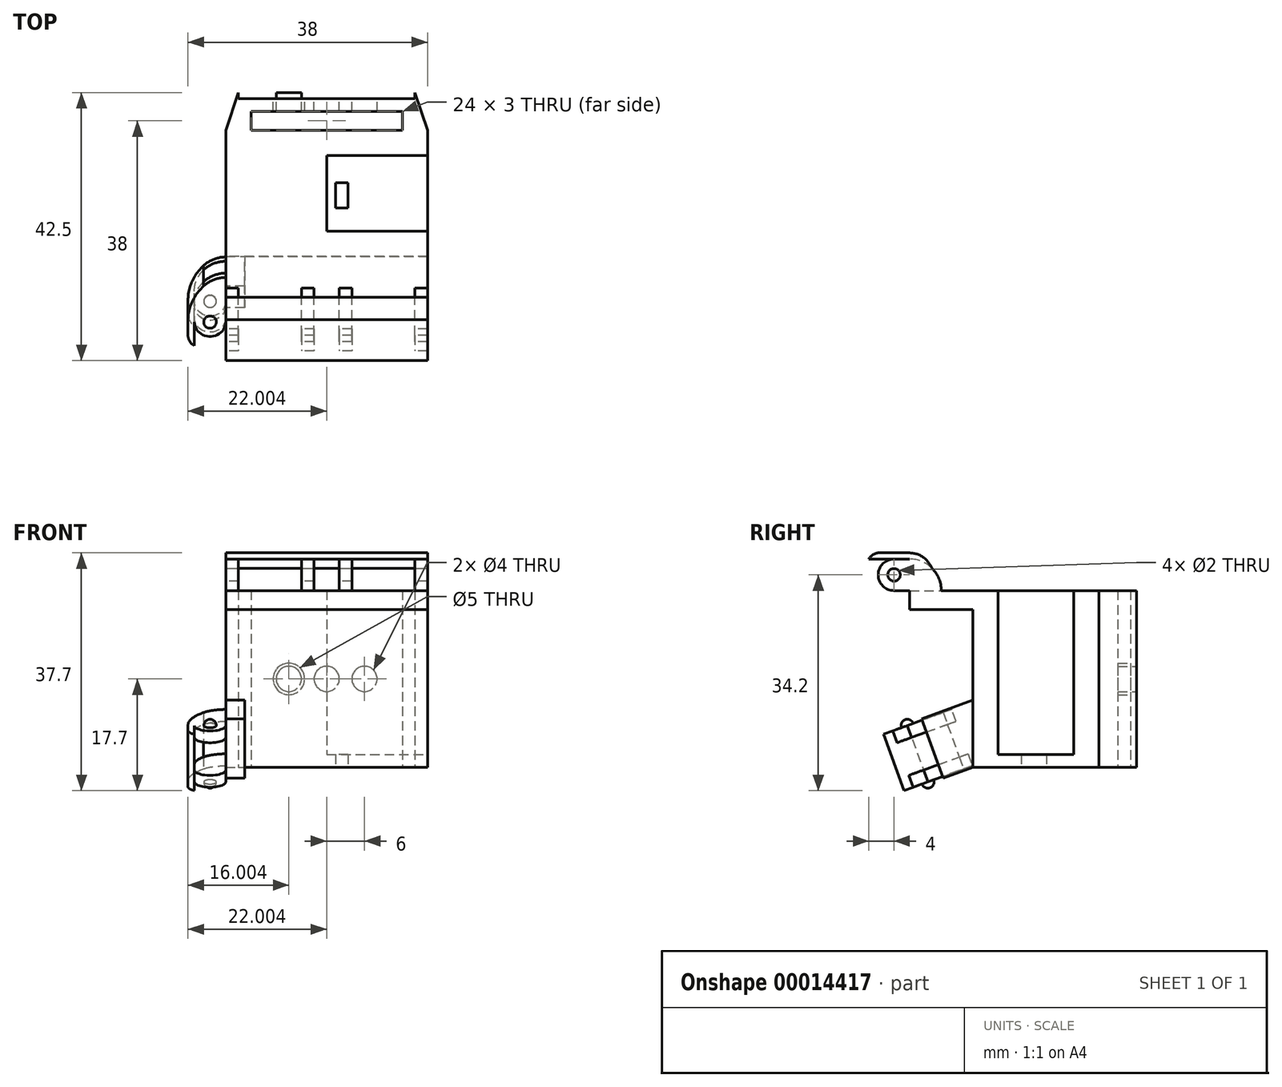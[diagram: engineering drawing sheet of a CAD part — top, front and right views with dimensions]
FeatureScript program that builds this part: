
annotation { "Feature Type Name" : "Feature", "Feature Type Description" : "" }
export const myFeature = defineFeature(function(context is Context, id is Id, definition is map)
    precondition{}
    {
        {
            var Q0;
            Q0=qCreatedBy(makeId("Top.planeOp"),FACE);
            var sketch = newSketch(context, id + "F0", { "sketchPlane" : qUnion([Q0])});
            skLineSegment(sketch, "E0.0", {"start": v(-15.62, 10.4) * mm, "end": v(16.38, 10.4) * mm});
            skLineSegment(sketch, "E0.1", {"start": v(-15.62, 10.4) * mm, "end": v(-15.62, -9.6) * mm});
            skLineSegment(sketch, "E0.2", {"start": v(-15.62, -9.6) * mm, "end": v(16.38, -9.6) * mm});
            skLineSegment(sketch, "E0.3", {"start": v(16.38, 10.4) * mm, "end": v(16.38, -9.6) * mm});
            skLineSegment(sketch, "E1", {"start": v(0.38, 10.4) * mm, "end": v(0.38, 16) * mm, "construction": true});
            skPoint(sketch, "E2", {"position": v(0.38, 13.4) * mm});
            skPoint(sketch, "E3", {"position": v(12.38, 10.4) * mm});
            skLineSegment(sketch, "E4", {"start": v(12.38, 10.4) * mm, "end": v(12.38, 13.4) * mm});
            skLineSegment(sketch, "E5", {"start": v(0.38, 13.4) * mm, "end": v(12.38, 13.4) * mm});
            skLineSegment(sketch, "E6.MirrorCS", {"start": v(0.38, 13.4) * mm, "end": v(-11.62, 13.4) * mm});
            skLineSegment(sketch, "E7.MirrorCS", {"start": v(-11.62, 10.4) * mm, "end": v(-11.62, 13.4) * mm});
            skPoint(sketch, "E8", {"position": v(0.38, 16.4) * mm});
            skLineSegment(sketch, "E9", {"start": v(0.38, 16.4) * mm, "end": v(14.38, 16.4) * mm});
            skLineSegment(sketch, "E10", {"start": v(16.38, 10.4) * mm, "end": v(14.38, 16.4) * mm});
            skLineSegment(sketch, "E11.MirrorCS", {"start": v(0.38, 16.4) * mm, "end": v(-13.62, 16.4) * mm});
            skLineSegment(sketch, "E12.MirrorCS", {"start": v(-15.62, 10.4) * mm, "end": v(-13.62, 16.4) * mm});
            skLineSegment(sketch, "E13", {"start": v(16.38, -5.6) * mm, "end": v(0.38, -5.6) * mm});
            skLineSegment(sketch, "E14", {"start": v(0.38, -5.6) * mm, "end": v(0.38, 6.4) * mm});
            skLineSegment(sketch, "E15", {"start": v(0.38, 6.4) * mm, "end": v(16.38, 6.4) * mm});
            skSolve(sketch);
        }
        {
            var Q0;
            {var subQ2=sQuery(id+"F0.wireOp",EDGE,"E4");Q0=makeQuery(id+"F0.imprint","IMPRINT",FACE,{"disambiguationData":[TD([[makeQuery(id+"F0.imprint","IMPRINT",EDGE,{"derivedFrom":subQ2}),-1.0]])]});}
            var Q1;
            {var subQ0=sQuery(id+"F0.wireOp",EDGE,"E0.1");Q1=makeQuery(id+"F0.imprint","IMPRINT",FACE,{"disambiguationData":[TD([[makeQuery(id+"F0.imprint","IMPRINT",EDGE,{"derivedFrom":subQ0}),1.0]])]});}
            extrude(context, id + "F1", {"entities" : qUnion([Q0, Q1]), "depth" : 28 * mm});
        }
        {
            var Q0;
            Q0=makeQuery(id+"F1.opExtrude","SWEPT_FACE",FACE,{"disambiguationData":[OSD([sQuery(id+"F0.wireOp",EDGE,"E9"),sQuery(id+"F0.wireOp",EDGE,"E11.MirrorCS")])]});
            var sketch = newSketch(context, id + "F2", { "sketchPlane" : qUnion([Q0])});
            skLineSegment(sketch, "E16", {"start": v(-14.88, 14) * mm, "end": v(14.12, 14) * mm, "construction": true});
            skCircle(sketch, "E17", {"center": v(-0.38, 14) * mm, "radius": 2.5 * mm});
            skCircle(sketch, "E18", {"center": v(-0.38, 14) * mm, "radius": 2 * mm});
            skCircle(sketch, "E19", {"center": v(-6.38, 14) * mm, "radius": 2.5 * mm});
            skCircle(sketch, "E20", {"center": v(-6.38, 14) * mm, "radius": 2 * mm});
            skPoint(sketch, "E21", {"position": v(-14.38, 0) * mm});
            skPoint(sketch, "E22", {"position": v(13.62, 0) * mm});
            skLineSegment(sketch, "E23", {"start": v(-14.38, 28) * mm, "end": v(13.62, 0) * mm, "construction": true});
            skLineSegment(sketch, "E24", {"start": v(-14.38, 0) * mm, "end": v(13.62, 28) * mm, "construction": true});
            skLineSegment(sketch, "E25", {"start": v(-0.38, 14) * mm, "end": v(-0.38, 1.54) * mm, "construction": true});
            skCircle(sketch, "E26.MirrorC", {"center": v(5.62, 14) * mm, "radius": 2.5 * mm});
            skCircle(sketch, "E27.MirrorC", {"center": v(5.62, 14) * mm, "radius": 2 * mm});
            skSolve(sketch);
        }
        {
            var Q0;
            Q0=makeQuery(id+"F2.imprint","IMPRINT",FACE,{"disambiguationData":[TD([[makeQuery(id+"F2.imprint","IMPRINT",EDGE,{"derivedFrom":sQuery(id+"F2.wireOp",EDGE,"E20")}),1.0]])]});
            var Q1;
            Q1=makeQuery(id+"F2.imprint","IMPRINT",FACE,{"disambiguationData":[TD([[makeQuery(id+"F2.imprint","IMPRINT",EDGE,{"derivedFrom":sQuery(id+"F2.wireOp",EDGE,"E18")}),1.0]])]});
            var Q2;
            Q2=makeQuery(id+"F2.imprint","IMPRINT",FACE,{"disambiguationData":[TD([[makeQuery(id+"F2.imprint","IMPRINT",EDGE,{"derivedFrom":sQuery(id+"F2.wireOp",EDGE,"20b49b63-29a2-4340-95f1-9f9b38b9fdb5.MirrorC")}),-1.0]])]});
            var Q3;
            Q3=makeQuery(id+"F2.imprint","IMPRINT",FACE,{"disambiguationData":[TD([[makeQuery(id+"F2.imprint","IMPRINT",EDGE,{"derivedFrom":sQuery(id+"F2.wireOp",EDGE,"E27.MirrorC")}),-1.0]])]});
            extrude(context, id + "F3", {"entities" : qUnion([Q0, Q1, Q2, Q3]), "operationType" : NewBodyOperationType.REMOVE, "endBound" : BoundingType.UP_TO_NEXT, "oppositeDirection" : true, "depth" : 25 * mm});
        }
        {
            var Q0;
            Q0=makeQuery(id+"F2.imprint","IMPRINT",FACE,{"disambiguationData":[TD([[makeQuery(id+"F2.imprint","IMPRINT",EDGE,{"derivedFrom":sQuery(id+"F2.wireOp",EDGE,"E19")}),1.0]])]});
            var Q1;
            Q1=makeQuery(id+"F2.imprint","IMPRINT",FACE,{"disambiguationData":[TD([[makeQuery(id+"F2.imprint","IMPRINT",EDGE,{"derivedFrom":sQuery(id+"F2.wireOp",EDGE,"64aa98c8-5af2-4ddf-8823-6346176a8d9f.MirrorC")}),-1.0]])]});
            var Q2;
            Q2=makeQuery(id+"F2.imprint","IMPRINT",FACE,{"disambiguationData":[TD([[makeQuery(id+"F2.imprint","IMPRINT",EDGE,{"derivedFrom":sQuery(id+"F2.wireOp",EDGE,"E17")}),1.0]])]});
            var Q3;
            Q3=makeQuery(id+"F2.imprint","IMPRINT",FACE,{"disambiguationData":[TD([[makeQuery(id+"F2.imprint","IMPRINT",EDGE,{"derivedFrom":sQuery(id+"F2.wireOp",EDGE,"E26.MirrorC")}),-1.0]])]});
            extrude(context, id + "F4", {"entities" : qUnion([Q0, Q1, Q2, Q3]), "operationType" : NewBodyOperationType.REMOVE, "oppositeDirection" : true, "depth" : 1 * mm});
        }
        {
            var Q0;
            Q0=makeQuery(id+"F1.opExtrude","SWEPT_FACE",FACE,{"disambiguationData":[OSD([sQuery(id+"F0.wireOp",EDGE,"E0.2")])]});
            var sketch = newSketch(context, id + "F5", { "sketchPlane" : qUnion([Q0])});
            skPoint(sketch, "E28", {"position": v(-15.62, 28) * mm});
            skPoint(sketch, "E29", {"position": v(-15.62, 25) * mm});
            skPoint(sketch, "E30", {"position": v(-12.62, 28) * mm});
            skLineSegment(sketch, "E31", {"start": v(-12.62, 28) * mm, "end": v(-12.62, 0) * mm, "construction": true});
            skLineSegment(sketch, "E32", {"start": v(-15.62, 25) * mm, "end": v(16.38, 25) * mm, "construction": true});
            skPoint(sketch, "E33", {"position": v(-12.62, 25) * mm});
            skLineSegment(sketch, "E34", {"start": v(16.38, 25) * mm, "end": v(-12.62, 25) * mm});
            skLineSegment(sketch, "E35", {"start": v(-12.62, 0) * mm, "end": v(-12.62, 25) * mm});
            skLineSegment(sketch, "E36", {"start": v(-15.62, 0) * mm, "end": v(-12.62, 0) * mm});
            skLineSegment(sketch, "E37", {"start": v(-15.62, 0) * mm, "end": v(-15.62, 28) * mm});
            skLineSegment(sketch, "E38", {"start": v(-15.62, 28) * mm, "end": v(16.38, 28) * mm});
            skLineSegment(sketch, "E39", {"start": v(16.38, 28) * mm, "end": v(16.38, 25) * mm});
            skSolve(sketch);
        }
        {
            var Q0;
            Q0=makeQuery(id+"F5.imprint","IMPRINT",FACE,{"disambiguationData":[TD([[makeQuery(id+"F5.imprint","IMPRINT",EDGE,{"derivedFrom":sQuery(id+"F5.wireOp",EDGE,"E34")}),-1.0]])]});
            extrude(context, id + "F6", {"entities" : qUnion([Q0]), "operationType" : NewBodyOperationType.ADD, "depth" : 10 * mm});
        }
        {
            var Q0;
            Q0=makeQuery(id+"F6.boolean.opBoolean","MERGE",FACE,{"derivedFrom":[makeQuery(id+"F1.opExtrude","CAP_FACE",FACE,{"disambiguationData":[OSD([sQuery(id+"F0.wireOp",EDGE,"a3dd4650-fcea-4df7-9243-878c2499c2b6.bottom"),sQuery(id+"F0.wireOp",EDGE,"a3dd4650-fcea-4df7-9243-878c2499c2b6.top"),sQuery(id+"F0.wireOp",EDGE,"a3dd4650-fcea-4df7-9243-878c2499c2b6.left"),sQuery(id+"F0.wireOp",EDGE,"a3dd4650-fcea-4df7-9243-878c2499c2b6.right"),sQuery(id+"F0.wireOp",EDGE,"E0.0"),sQuery(id+"F0.wireOp",EDGE,"E0.1"),sQuery(id+"F0.wireOp",EDGE,"E0.2"),sQuery(id+"F0.wireOp",EDGE,"E0.3"),sQuery(id+"F0.wireOp",EDGE,"E4"),sQuery(id+"F0.wireOp",EDGE,"E5"),sQuery(id+"F0.wireOp",EDGE,"E6.MirrorCS"),sQuery(id+"F0.wireOp",EDGE,"E7.MirrorCS"),sQuery(id+"F0.wireOp",EDGE,"E9"),sQuery(id+"F0.wireOp",EDGE,"E10"),sQuery(id+"F0.wireOp",EDGE,"E11.MirrorCS"),sQuery(id+"F0.wireOp",EDGE,"E12.MirrorCS")])],"isStart":false}),makeQuery(id+"F6.opExtrude","SWEPT_FACE",FACE,{"disambiguationData":[OSD([sQuery(id+"F5.wireOp",EDGE,"E38")])]})]});
            var sketch = newSketch(context, id + "F7", { "sketchPlane" : qUnion([Q0])});
            skPoint(sketch, "E40", {"position": v(-15.62, -19.6) * mm});
            skPoint(sketch, "E41", {"position": v(-13.62, -19.6) * mm});
            skPoint(sketch, "E42", {"position": v(0.38, -19.6) * mm});
            skLineSegment(sketch, "E43", {"start": v(-15.62, -19.6) * mm, "end": v(-15.62, -24.6) * mm, "construction": true});
            skLineSegment(sketch, "E44", {"start": v(-13.62, -19.6) * mm, "end": v(-13.62, -24.6) * mm, "construction": true});
            skLineSegment(sketch, "E45", {"start": v(-15.62, -19.6) * mm, "end": v(-15.62, -14.6) * mm, "construction": true});
            skLineSegment(sketch, "E46", {"start": v(-13.62, -19.6) * mm, "end": v(-13.62, -14.6) * mm, "construction": true});
            skLineSegment(sketch, "E47", {"start": v(-15.62, -14.6) * mm, "end": v(-13.62, -14.6) * mm});
            skLineSegment(sketch, "E48", {"start": v(-13.62, -24.6) * mm, "end": v(-13.62, -14.6) * mm});
            skLineSegment(sketch, "E49", {"start": v(-15.62, -24.6) * mm, "end": v(-15.62, -14.6) * mm});
            skLineSegment(sketch, "E50", {"start": v(-15.62, -24.6) * mm, "end": v(-13.62, -24.6) * mm});
            skLineSegment(sketch, "E51", {"start": v(0.38, -19.6) * mm, "end": v(0.38, -13.68) * mm, "construction": true});
            skLineSegment(sketch, "E52.MirrorCS", {"start": v(14.38, -24.6) * mm, "end": v(14.38, -14.6) * mm});
            skLineSegment(sketch, "E53.MirrorCS", {"start": v(16.38, -24.6) * mm, "end": v(16.38, -14.6) * mm});
            skLineSegment(sketch, "E54.MirrorCS", {"start": v(16.38, -14.6) * mm, "end": v(14.38, -14.6) * mm});
            skLineSegment(sketch, "E55.MirrorCS", {"start": v(16.38, -24.6) * mm, "end": v(14.38, -24.6) * mm});
            skPoint(sketch, "E56", {"position": v(-8.62, -19.6) * mm});
            skLineSegment(sketch, "E57", {"start": v(-8.62, -19.6) * mm, "end": v(-8.62, -14.6) * mm, "construction": true});
            skLineSegment(sketch, "E58.MirrorCS", {"start": v(-1.62, -24.6) * mm, "end": v(-1.62, -14.6) * mm});
            skLineSegment(sketch, "E59.MirrorCS", {"start": v(-3.62, -24.6) * mm, "end": v(-3.62, -14.6) * mm});
            skLineSegment(sketch, "E60.MirrorCS", {"start": v(-1.62, -24.6) * mm, "end": v(-3.62, -24.6) * mm});
            skLineSegment(sketch, "E61.MirrorCS", {"start": v(-1.62, -14.6) * mm, "end": v(-3.62, -14.6) * mm});
            skLineSegment(sketch, "E62.MirrorCS", {"start": v(2.38, -24.6) * mm, "end": v(2.38, -14.6) * mm});
            skLineSegment(sketch, "E63.MirrorCS", {"start": v(4.38, -24.6) * mm, "end": v(4.38, -14.6) * mm});
            skLineSegment(sketch, "E64.MirrorCS", {"start": v(2.38, -14.6) * mm, "end": v(4.38, -14.6) * mm});
            skLineSegment(sketch, "E65.MirrorCS", {"start": v(2.38, -24.6) * mm, "end": v(4.38, -24.6) * mm});
            skSolve(sketch);
        }
        {
            var Q0;
            {var subQ5=sQuery(id+"F7.wireOp",EDGE,"E47");Q0=makeQuery(id+"F7.imprint","IMPRINT",FACE,{"disambiguationData":[TD([[makeQuery(id+"F7.imprint","IMPRINT",EDGE,{"derivedFrom":subQ5}),-1.0]])]});}
            var Q1;
            {var subQ5=sQuery(id+"F7.wireOp",EDGE,"E50");Q1=makeQuery(id+"F7.imprint","IMPRINT",FACE,{"disambiguationData":[TD([[makeQuery(id+"F7.imprint","IMPRINT",EDGE,{"derivedFrom":subQ5}),1.0]])]});}
            var Q2;
            {var subQ5=sQuery(id+"F7.wireOp",EDGE,"E55.MirrorCS");Q2=makeQuery(id+"F7.imprint","IMPRINT",FACE,{"disambiguationData":[TD([[makeQuery(id+"F7.imprint","IMPRINT",EDGE,{"derivedFrom":subQ5}),-1.0]])]});}
            var Q3;
            {var subQ0=sQuery(id+"F7.wireOp",EDGE,"E54.MirrorCS");Q3=makeQuery(id+"F7.imprint","IMPRINT",FACE,{"disambiguationData":[TD([[makeQuery(id+"F7.imprint","IMPRINT",EDGE,{"derivedFrom":subQ0}),1.0]])]});}
            var Q4;
            {var subQ5=sQuery(id+"F7.wireOp",EDGE,"E61.MirrorCS");Q4=makeQuery(id+"F7.imprint","IMPRINT",FACE,{"disambiguationData":[TD([[makeQuery(id+"F7.imprint","IMPRINT",EDGE,{"derivedFrom":subQ5}),1.0]])]});}
            var Q5;
            {var subQ5=sQuery(id+"F7.wireOp",EDGE,"E60.MirrorCS");Q5=makeQuery(id+"F7.imprint","IMPRINT",FACE,{"disambiguationData":[TD([[makeQuery(id+"F7.imprint","IMPRINT",EDGE,{"derivedFrom":subQ5}),-1.0]])]});}
            var Q6;
            {var subQ0=sQuery(id+"F7.wireOp",EDGE,"E64.MirrorCS");Q6=makeQuery(id+"F7.imprint","IMPRINT",FACE,{"disambiguationData":[TD([[makeQuery(id+"F7.imprint","IMPRINT",EDGE,{"derivedFrom":subQ0}),-1.0]])]});}
            var Q7;
            {var subQ5=sQuery(id+"F7.wireOp",EDGE,"E65.MirrorCS");Q7=makeQuery(id+"F7.imprint","IMPRINT",FACE,{"disambiguationData":[TD([[makeQuery(id+"F7.imprint","IMPRINT",EDGE,{"derivedFrom":subQ5}),1.0]])]});}
            extrude(context, id + "F8", {"entities" : qUnion([Q0, Q1, Q2, Q3, Q4, Q5, Q6, Q7]), "operationType" : NewBodyOperationType.ADD, "depth" : 5 * mm});
        }
        {
            var Q0;
            Q0=makeQuery(id+"F6.opExtrude","CAP_FACE",FACE,{"disambiguationData":[OSD([sQuery(id+"F5.wireOp",EDGE,"E34"),sQuery(id+"F5.wireOp",EDGE,"E35"),sQuery(id+"F5.wireOp",EDGE,"E36"),sQuery(id+"F5.wireOp",EDGE,"E37"),sQuery(id+"F5.wireOp",EDGE,"E38"),sQuery(id+"F5.wireOp",EDGE,"E39")])],"isStart":false});
            var sketch = newSketch(context, id + "F9", { "sketchPlane" : qUnion([Q0])});
            skPoint(sketch, "E66", {"position": v(-12.62, 25) * mm});
            skLineSegment(sketch, "E67", {"start": v(-12.62, 25) * mm, "end": v(-15.62, 25) * mm});
            skSolve(sketch);
        }
        {
            var Q0;
            {var subQ1=sQuery(id+"F9.wireOp",EDGE,"E67");Q0=makeQuery(id+"F9.imprint","IMPRINT",FACE,{"disambiguationData":[TD([[makeQuery(id+"F9.imprint","IMPRINT",EDGE,{"derivedFrom":subQ1}),1.0]])]});}
            extrude(context, id + "F10", {"entities" : qUnion([Q0]), "operationType" : NewBodyOperationType.REMOVE, "oppositeDirection" : true, "depth" : 10 * mm});
        }
        {
            var Q0;
            Q0=makeQuery(id+"F6.boolean.opBoolean","MERGE",FACE,{"derivedFrom":[makeQuery(id+"F1.opExtrude","SWEPT_FACE",FACE,{"disambiguationData":[OSD([sQuery(id+"F0.wireOp",EDGE,"E0.1")])]}),makeQuery(id+"F6.opExtrude","SWEPT_FACE",FACE,{"disambiguationData":[OSD([sQuery(id+"F5.wireOp",EDGE,"E37")])]})]});
            var sketch = newSketch(context, id + "F11", { "sketchPlane" : qUnion([Q0])});
            skPoint(sketch, "E68", {"position": v(9.6, 0) * mm});
            skPoint(sketch, "E69", {"position": v(9.6, 25) * mm});
            skPoint(sketch, "E70", {"position": v(9.6, 12.5) * mm});
            skLineSegment(sketch, "E71", {"start": v(9.6, 0) * mm, "end": v(14.3, -1.71) * mm, "construction": true});
            skLineSegment(sketch, "E72", {"start": v(9.6, 0) * mm, "end": v(9.6, 12.5) * mm, "construction": true});
            skLineSegment(sketch, "E73", {"start": v(14.3, -1.71) * mm, "end": v(17.72, 7.69) * mm, "construction": true});
            skLineSegment(sketch, "E74", {"start": v(17.72, 7.69) * mm, "end": v(9.6, 10.64) * mm, "construction": true});
            skLineSegment(sketch, "E75", {"start": v(9.6, 10.64) * mm, "end": v(17.72, 7.69) * mm});
            skLineSegment(sketch, "E76", {"start": v(17.72, 7.69) * mm, "end": v(14.3, -1.71) * mm});
            skLineSegment(sketch, "E77", {"start": v(14.3, -1.71) * mm, "end": v(9.6, 0) * mm});
            skLineSegment(sketch, "E78", {"start": v(9.6, 0) * mm, "end": v(9.6, 10.64) * mm});
            skSolve(sketch);
        }
        {
            var Q0;
            Q0=makeQuery(id+"F11.imprint","IMPRINT",FACE,{"disambiguationData":[TD([[makeQuery(id+"F11.imprint","IMPRINT",EDGE,{"derivedFrom":sQuery(id+"F11.wireOp",EDGE,"E75")}),-1.0]])]});
            extrude(context, id + "F12", {"entities" : qUnion([Q0]), "operationType" : NewBodyOperationType.ADD, "oppositeDirection" : true, "depth" : 3 * mm});
        }
        {
            var Q0;
            Q0=makeQuery(id+"F12.boolean.opBoolean","MERGE",FACE,{"derivedFrom":[makeQuery(id+"F6.boolean.opBoolean","MERGE",FACE,{"derivedFrom":[makeQuery(id+"F1.opExtrude","SWEPT_FACE",FACE,{"disambiguationData":[OSD([sQuery(id+"F0.wireOp",EDGE,"E0.1")])]}),makeQuery(id+"F6.opExtrude","SWEPT_FACE",FACE,{"disambiguationData":[OSD([sQuery(id+"F5.wireOp",EDGE,"E37")])]})]}),makeQuery(id+"F12.opExtrude","CAP_FACE",FACE,{"disambiguationData":[OSD([sQuery(id+"F11.wireOp",EDGE,"E75"),sQuery(id+"F11.wireOp",EDGE,"E76"),sQuery(id+"F11.wireOp",EDGE,"E77"),sQuery(id+"F11.wireOp",EDGE,"E78")])],"isStart":true})]});
            var sketch = newSketch(context, id + "F13", { "sketchPlane" : qUnion([Q0])});
            skPoint(sketch, "E79", {"position": v(17.72, 7.69) * mm});
            skPoint(sketch, "E80", {"position": v(16, 2.99) * mm});
            skPoint(sketch, "E81", {"position": v(16.95, 5.57) * mm});
            skLineSegment(sketch, "E82", {"start": v(16, 2.99) * mm, "end": v(13.28, 3.98) * mm, "construction": true});
            skLineSegment(sketch, "E83", {"start": v(17.72, 7.69) * mm, "end": v(22.42, 5.98) * mm, "construction": true});
            skLineSegment(sketch, "E84", {"start": v(16.95, 5.57) * mm, "end": v(21.65, 3.86) * mm, "construction": true});
            skLineSegment(sketch, "E85", {"start": v(21.65, 3.86) * mm, "end": v(16.95, 5.57) * mm});
            skPoint(sketch, "E86", {"position": v(13.02, 9.4) * mm});
            skLineSegment(sketch, "E87", {"start": v(21.65, 3.86) * mm, "end": v(12.25, 7.28) * mm});
            skLineSegment(sketch, "E88.MirrorCS", {"start": v(19.77, -1.3) * mm, "end": v(10.37, 2.11) * mm});
            skLineSegment(sketch, "E89", {"start": v(12.25, 7.28) * mm, "end": v(12.93, 9.16) * mm});
            skLineSegment(sketch, "E90.MirrorCS", {"start": v(21.65, 3.86) * mm, "end": v(22.33, 5.74) * mm});
            skLineSegment(sketch, "E91", {"start": v(12.93, 9.16) * mm, "end": v(22.33, 5.74) * mm});
            skLineSegment(sketch, "E92.MirrorCS", {"start": v(10.37, 2.11) * mm, "end": v(9.69, 0.23) * mm});
            skLineSegment(sketch, "E93.MirrorCS", {"start": v(9.69, 0.23) * mm, "end": v(19.08, -3.19) * mm});
            skLineSegment(sketch, "E94.MirrorCS", {"start": v(19.77, -1.3) * mm, "end": v(19.08, -3.19) * mm});
            skSolve(sketch);
        }
        {
            var Q0;
            {var subQ1=sQuery(id+"F13.wireOp",EDGE,"27cdea62-a975-46e6-88ea-ef7a49258366");Q0=makeQuery(id+"F13.imprint","IMPRINT",FACE,{"disambiguationData":[TD([[makeQuery(id+"F13.imprint","IMPRINT",EDGE,{"derivedFrom":subQ1}),-1.0]])]});}
            var Q1;
            {var subQ3=sQuery(id+"F13.wireOp",EDGE,"4966c16b-bf24-40fc-986f-31c6d37c2082");Q1=makeQuery(id+"F13.imprint","IMPRINT",FACE,{"disambiguationData":[TD([[makeQuery(id+"F13.imprint","IMPRINT",EDGE,{"derivedFrom":subQ3}),-1.0]])]});}
            var Q2;
            {var subQ4=sQuery(id+"F13.wireOp",EDGE,"a727023f-dfa3-4c32-8afa-23e3bec39dac0.MirrorCS");Q2=makeQuery(id+"F13.imprint","IMPRINT",FACE,{"disambiguationData":[TD([[makeQuery(id+"F13.imprint","IMPRINT",EDGE,{"derivedFrom":subQ4}),1.0]])]});}
            var Q3;
            {var subQ3=sQuery(id+"F13.wireOp",EDGE,"6426e7fb-16d1-409e-b700-4e2e672a5eb60.MirrorCS");Q3=makeQuery(id+"F13.imprint","IMPRINT",FACE,{"disambiguationData":[TD([[makeQuery(id+"F13.imprint","IMPRINT",EDGE,{"derivedFrom":subQ3}),1.0]])]});}
            var Q4;
            {var subQ5=sQuery(id+"F13.wireOp",EDGE,"E89");Q4=makeQuery(id+"F13.imprint","IMPRINT",FACE,{"disambiguationData":[TD([[makeQuery(id+"F13.imprint","IMPRINT",EDGE,{"derivedFrom":subQ5}),-1.0]])]});}
            var Q5;
            {var subQ5=sQuery(id+"F13.wireOp",EDGE,"E90.MirrorCS");Q5=makeQuery(id+"F13.imprint","IMPRINT",FACE,{"disambiguationData":[TD([[makeQuery(id+"F13.imprint","IMPRINT",EDGE,{"derivedFrom":subQ5}),1.0]])]});}
            var Q6;
            {var subQ5=sQuery(id+"F13.wireOp",EDGE,"E92.MirrorCS");Q6=makeQuery(id+"F13.imprint","IMPRINT",FACE,{"disambiguationData":[TD([[makeQuery(id+"F13.imprint","IMPRINT",EDGE,{"derivedFrom":subQ5}),1.0]])]});}
            var Q7;
            {var subQ5=sQuery(id+"F13.wireOp",EDGE,"E94.MirrorCS");Q7=makeQuery(id+"F13.imprint","IMPRINT",FACE,{"disambiguationData":[TD([[makeQuery(id+"F13.imprint","IMPRINT",EDGE,{"derivedFrom":subQ5}),-1.0]])]});}
            extrude(context, id + "F14", {"entities" : qUnion([Q0, Q1, Q2, Q3, Q4, Q5, Q6, Q7]), "operationType" : NewBodyOperationType.ADD, "depth" : 5 * mm});
        }
        {
            var Q0;
            Q0=makeQuery(id+"F14.opExtrude","SWEPT_FACE",FACE,{"disambiguationData":[OSD([sQuery(id+"F13.wireOp",EDGE,"E93.MirrorCS")])]});
            var sketch = newSketch(context, id + "F15", { "sketchPlane" : qUnion([Q0])});
            skPoint(sketch, "E95", {"position": v(-15.62, 14.02) * mm});
            skPoint(sketch, "E96", {"position": v(-15.62, 19.02) * mm});
            skPoint(sketch, "E97", {"position": v(-20.62, 19.02) * mm});
            skPoint(sketch, "E98", {"position": v(-20.62, 14.02) * mm});
            skLineSegment(sketch, "E99", {"start": v(-20.62, 19.02) * mm, "end": v(-15.62, 14.02) * mm, "construction": true});
            skLineSegment(sketch, "E100", {"start": v(-20.62, 14.02) * mm, "end": v(-15.62, 19.02) * mm, "construction": true});
            skLineSegment(sketch, "E101", {"start": v(-15.62, 16.52) * mm, "end": v(-20.62, 16.52) * mm, "construction": true});
            skCircle(sketch, "E102", {"center": v(-18.12, 16.52) * mm, "radius": 1 * mm});
            skPoint(sketch, "E103", {"position": v(-15.62, 9.02) * mm});
            skArc(sketch, "E104", {"start": v(-20.62, 14.02) * mm, "mid": v(-19.15, 10.49) * mm, "end": v(-15.62, 9.02) * mm});
            skArc(sketch, "E105", {"start": v(-15.62, 16.52) * mm, "mid": v(-18.12, 19) * mm, "end": v(-20.62, 16.52) * mm});
            skLineSegment(sketch, "E106", {"start": v(-20.62, 14.02) * mm, "end": v(-20.62, 16.52) * mm});
            skLineSegment(sketch, "E107", {"start": v(-15.62, 16.52) * mm, "end": v(-15.62, 14.02) * mm});
            skLineSegment(sketch, "E108", {"start": v(-20.62, 16.52) * mm, "end": v(-20.62, 20.52) * mm});
            skLineSegment(sketch, "E109", {"start": v(-20.62, 20.52) * mm, "end": v(-21.62, 20.52) * mm});
            skLineSegment(sketch, "E110", {"start": v(-21.62, 16.52) * mm, "end": v(-21.62, 20.52) * mm});
            skFitSpline(sketch, "E111", {"points": [v(-21.62, 16.52) * mm, v(-19.15, 10.49) * mm], "startDerivative": vector(-0.1, -6.77) * mm, "endDerivative": vector(5.11, -4.97) * mm});
            skSolve(sketch);
        }
        {
            var Q0;
            Q0=makeQuery(id+"F14.opExtrude","SWEPT_FACE",FACE,{"disambiguationData":[OSD([sQuery(id+"F13.wireOp",EDGE,"E91")])]});
            var sketch = newSketch(context, id + "F16", { "sketchPlane" : qUnion([Q0])});
            skPoint(sketch, "E112", {"position": v(-15.62, -19.02) * mm});
            skPoint(sketch, "E113", {"position": v(-15.62, -14.02) * mm});
            skPoint(sketch, "E114", {"position": v(-20.62, -19.02) * mm});
            skPoint(sketch, "E115", {"position": v(-20.62, -14.02) * mm});
            skLineSegment(sketch, "E116", {"start": v(-20.62, -14.02) * mm, "end": v(-15.62, -19.02) * mm, "construction": true});
            skLineSegment(sketch, "E117", {"start": v(-20.62, -19.02) * mm, "end": v(-15.62, -14.02) * mm, "construction": true});
            skCircle(sketch, "E118", {"center": v(-18.12, -16.52) * mm, "radius": 1 * mm});
            skSolve(sketch);
        }
        {
            var Q0;
            Q0=makeQuery(id+"F16.imprint","IMPRINT",FACE,{"disambiguationData":[TD([[makeQuery(id+"F16.imprint","IMPRINT",EDGE,{"derivedFrom":sQuery(id+"F16.wireOp",EDGE,"E118")}),1.0]])]});
            extrude(context, id + "F17", {"entities" : qUnion([Q0]), "operationType" : NewBodyOperationType.ADD, "depth" : 1 * mm});
        }
        {
            var Q0;
            Q0=makeQuery(id+"F15.imprint","IMPRINT",FACE,{"disambiguationData":[TD([[makeQuery(id+"F15.imprint","IMPRINT",EDGE,{"derivedFrom":sQuery(id+"F15.wireOp",EDGE,"E102")}),1.0]])]});
            extrude(context, id + "F18", {"entities" : qUnion([Q0]), "operationType" : NewBodyOperationType.ADD, "depth" : 1 * mm});
        }
        {
            var Q0;
            {var subQ3=sQuery(id+"F15.wireOp",EDGE,"E105");Q0=makeQuery(id+"F15.imprint","IMPRINT",FACE,{"disambiguationData":[TD([[makeQuery(id+"F15.imprint","IMPRINT",EDGE,{"derivedFrom":subQ3}),-1.0]])]});}
            var Q1;
            {var subQ2=sQuery(id+"F15.wireOp",EDGE,"E104");Q1=makeQuery(id+"F15.imprint","IMPRINT",FACE,{"disambiguationData":[TD([[makeQuery(id+"F15.imprint","IMPRINT",EDGE,{"derivedFrom":subQ2}),-1.0]])]});}
            extrude(context, id + "F19", {"entities" : qUnion([Q0, Q1]), "operationType" : NewBodyOperationType.REMOVE, "endBound" : BoundingType.THROUGH_ALL, "oppositeDirection" : true, "depth" : 25 * mm});
        }
        {
            var Q0;
            Q0=makeQuery(id+"F12.boolean.opBoolean","MERGE",FACE,{"derivedFrom":[makeQuery(id+"F8.boolean.opBoolean","MERGE",FACE,{"derivedFrom":[makeQuery(id+"F6.boolean.opBoolean","MERGE",FACE,{"derivedFrom":[makeQuery(id+"F1.opExtrude","SWEPT_FACE",FACE,{"disambiguationData":[OSD([sQuery(id+"F0.wireOp",EDGE,"E0.1")])]}),makeQuery(id+"F6.opExtrude","SWEPT_FACE",FACE,{"disambiguationData":[OSD([sQuery(id+"F5.wireOp",EDGE,"E37")])]})]}),makeQuery(id+"F8.opExtrude","SWEPT_FACE",FACE,{"disambiguationData":[OSD([sQuery(id+"F7.wireOp",EDGE,"E49")])]})]}),makeQuery(id+"F12.opExtrude","CAP_FACE",FACE,{"disambiguationData":[OSD([sQuery(id+"F11.wireOp",EDGE,"E75"),sQuery(id+"F11.wireOp",EDGE,"E76"),sQuery(id+"F11.wireOp",EDGE,"E77"),sQuery(id+"F11.wireOp",EDGE,"E78")])],"isStart":true})]});
            var sketch = newSketch(context, id + "F20", { "sketchPlane" : qUnion([Q0])});
            skPoint(sketch, "E119", {"position": v(19.6, 28) * mm});
            skPoint(sketch, "E120", {"position": v(24.6, 33) * mm});
            skPoint(sketch, "E121", {"position": v(24.6, 28) * mm});
            skLineSegment(sketch, "E122", {"start": v(19.6, 28) * mm, "end": v(19.6, 33) * mm, "construction": true});
            skLineSegment(sketch, "E123", {"start": v(19.6, 33) * mm, "end": v(24.6, 28) * mm, "construction": true});
            skLineSegment(sketch, "E124", {"start": v(19.6, 28) * mm, "end": v(24.6, 33) * mm, "construction": true});
            skPoint(sketch, "E125", {"position": v(22.1, 30.5) * mm});
            skCircle(sketch, "E126", {"center": v(22.1, 30.5) * mm, "radius": 1 * mm});
            skPoint(sketch, "E127", {"position": v(14.6, 28) * mm});
            skArc(sketch, "E128", {"start": v(19.6, 33) * mm, "mid": v(16.06, 31.54) * mm, "end": v(14.6, 28) * mm});
            skPoint(sketch, "E129", {"position": v(22.1, 33) * mm});
            skPoint(sketch, "E130", {"position": v(22.1, 28) * mm});
            skArc(sketch, "E131", {"start": v(22.1, 28) * mm, "mid": v(24.6, 30.5) * mm, "end": v(22.1, 33) * mm});
            skLineSegment(sketch, "E132", {"start": v(19.6, 28) * mm, "end": v(19.6, 33) * mm});
            skLineSegment(sketch, "E133", {"start": v(22.1, 33) * mm, "end": v(19.6, 33) * mm});
            skLineSegment(sketch, "E134", {"start": v(19.6, 28) * mm, "end": v(22.1, 28) * mm});
            skSolve(sketch);
        }
        {
            var Q0;
            {var subQ2=sQuery(id+"F20.wireOp",EDGE,"E128");Q0=makeQuery(id+"F20.imprint","IMPRINT",FACE,{"disambiguationData":[TD([[makeQuery(id+"F20.imprint","IMPRINT",EDGE,{"derivedFrom":subQ2}),-1.0]])]});}
            var Q1;
            {var subQ0=sQuery(id+"F20.wireOp",EDGE,"E131");var subQ1=sQuery(id+"F7.wireOp",EDGE,"E49");var subQ2=makeQuery(id+"F8.opExtrude","CAP_EDGE",EDGE,{"disambiguationData":[OSD([subQ1])],"isStart":false});var subQ3=makeQuery(id+"F20.imprint","INTERSECT",VERTEX,{"derivedFrom":[subQ2,subQ0,sQuery(id+"F20.wireOp",EDGE,"E133")]});Q1=makeQuery(id+"F20.imprint","IMPRINT",FACE,{"disambiguationData":[TD([[makeQuery(id+"F20.imprint","IMPRINT",EDGE,{"disambiguationData":[TD([[subQ3,1.0]])],"derivedFrom":subQ0}),-1.0]])]});}
            var Q2;
            {var subQ0=sQuery(id+"F20.wireOp",EDGE,"E131");var subQ1=sQuery(id+"F7.wireOp",EDGE,"E49");var subQ2=makeQuery(id+"F8.opExtrude","CAP_EDGE",EDGE,{"disambiguationData":[OSD([subQ1])],"isStart":true});var subQ3=makeQuery(id+"F20.imprint","INTERSECT",VERTEX,{"derivedFrom":[subQ2,subQ0,sQuery(id+"F20.wireOp",EDGE,"E134")]});Q2=makeQuery(id+"F20.imprint","IMPRINT",FACE,{"disambiguationData":[TD([[makeQuery(id+"F20.imprint","IMPRINT",EDGE,{"disambiguationData":[TD([[subQ3,-1.0]])],"derivedFrom":subQ0}),-1.0]])]});}
            var Q3;
            Q3=makeQuery(id+"F20.imprint","IMPRINT",FACE,{"disambiguationData":[TD([[makeQuery(id+"F20.imprint","IMPRINT",EDGE,{"derivedFrom":sQuery(id+"F20.wireOp",EDGE,"E126")}),1.0]])]});
            extrude(context, id + "F21", {"entities" : qUnion([Q0, Q1, Q2, Q3]), "operationType" : NewBodyOperationType.REMOVE, "endBound" : BoundingType.THROUGH_ALL, "oppositeDirection" : true, "depth" : 25 * mm});
        }
        {
            var Q0;
            Q0=makeQuery(id+"F8.opExtrude","CAP_FACE",FACE,{"disambiguationData":[OSD([sQuery(id+"F7.wireOp",EDGE,"E47"),sQuery(id+"F7.wireOp",EDGE,"E48"),sQuery(id+"F7.wireOp",EDGE,"E50"),sQuery(id+"F7.wireOp",EDGE,"E49")])],"isStart":false});
            var sketch = newSketch(context, id + "F22", { "sketchPlane" : qUnion([Q0])});
            skPoint(sketch, "E135", {"position": v(-14.62, -19.6) * mm});
            skLineSegment(sketch, "E136", {"start": v(-14.62, -20.6) * mm, "end": v(-14.62, -24.6) * mm});
            skLineSegment(sketch, "E137", {"start": v(-14.62, -24.6) * mm, "end": v(-8.62, -24.6) * mm});
            skLineSegment(sketch, "E138", {"start": v(-8.62, -24.6) * mm, "end": v(-8.62, -20.6) * mm});
            skLineSegment(sketch, "E139", {"start": v(-13.62, -19.6) * mm, "end": v(-9.62, -19.6) * mm});
            skArc(sketch, "E140.filletArc", {"start": v(-13.62, -19.6) * mm, "mid": v(-14.32, -19.9) * mm, "end": v(-14.62, -20.6) * mm});
            skPoint(sketch, "E141.visualSharp", {"position": v(-8.62, -19.6) * mm});
            skArc(sketch, "E141.filletArc", {"start": v(-8.62, -20.6) * mm, "mid": v(-8.9, -19.9) * mm, "end": v(-9.62, -19.6) * mm});
            skSolve(sketch);
        }
        {
            var Q0;
            Q0=makeQuery(id+"F8.opExtrude","CAP_FACE",FACE,{"disambiguationData":[OSD([sQuery(id+"F7.wireOp",EDGE,"E62.MirrorCS"),sQuery(id+"F7.wireOp",EDGE,"E63.MirrorCS"),sQuery(id+"F7.wireOp",EDGE,"E64.MirrorCS"),sQuery(id+"F7.wireOp",EDGE,"E65.MirrorCS")])],"isStart":false});
            var sketch = newSketch(context, id + "F23", { "sketchPlane" : qUnion([Q0])});
            skPoint(sketch, "E142", {"position": v(3.38, -19.6) * mm});
            skLineSegment(sketch, "E143", {"start": v(3.38, -20.6) * mm, "end": v(3.38, -24.6) * mm});
            skLineSegment(sketch, "E144", {"start": v(3.38, -24.6) * mm, "end": v(9.38, -24.6) * mm});
            skLineSegment(sketch, "E145", {"start": v(9.38, -24.6) * mm, "end": v(9.38, -20.6) * mm});
            skLineSegment(sketch, "E146", {"start": v(4.38, -19.6) * mm, "end": v(8.38, -19.6) * mm});
            skArc(sketch, "E147.filletArc", {"start": v(4.38, -19.6) * mm, "mid": v(3.68, -19.9) * mm, "end": v(3.38, -20.6) * mm});
            skPoint(sketch, "E148.visualSharp", {"position": v(9.38, -19.6) * mm});
            skArc(sketch, "E148.filletArc", {"start": v(9.38, -20.6) * mm, "mid": v(9.1, -19.9) * mm, "end": v(8.38, -19.6) * mm});
            skSolve(sketch);
        }
        {
            var Q0;
            Q0=makeQuery(id+"F17.opExtrude","CAP_EDGE",EDGE,{"disambiguationData":[OSD([sQuery(id+"F16.wireOp",EDGE,"E118")])],"isStart":false});
            var Q1;
            Q1=makeQuery(id+"F18.opExtrude","CAP_EDGE",EDGE,{"disambiguationData":[OSD([sQuery(id+"F15.wireOp",EDGE,"E102")])],"isStart":false});
            fillet(context, id + "F24", {"entities" : qUnion([Q0, Q1]), "radius" : 1 * mm, "tangentPropagation" : true, "allowEdgeOverflow" : false});
        }
        {
            var Q0;
            Q0=makeQuery(id+"F1.opExtrude","SWEPT_FACE",FACE,{"disambiguationData":[OSD([sQuery(id+"F0.wireOp",EDGE,"E14")])]});
            var sketch = newSketch(context, id + "F25", { "sketchPlane" : qUnion([Q0])});
            skSolve(sketch);
        }
        {
            var Q0;
            {var subQ0=sQuery(id+"F0.wireOp",EDGE,"E14");Q0=makeQuery(id+"F25.imprint","IMPRINT",FACE,{"disambiguationData":[TD([[makeQuery(id+"F25.imprint","IMPRINT",EDGE,{"derivedFrom":makeQuery(id+"F1.opExtrude","CAP_EDGE",EDGE,{"disambiguationData":[OSD([subQ0])],"isStart":true})}),1.0]])]});}
            var sketch = newSketch(context, id + "F26", { "sketchPlane" : qUnion([Q0])});
            skPoint(sketch, "E149", {"position": v(6.4, 0) * mm});
            skPoint(sketch, "E150", {"position": v(0, 0) * mm});
            skPoint(sketch, "E151", {"position": v(6.4, 2) * mm});
            skLineSegment(sketch, "E152", {"start": v(6.4, 2) * mm, "end": v(-5.63, 2) * mm});
            skLineSegment(sketch, "E153", {"start": v(-5.63, 2) * mm, "end": v(-5.63, 0) * mm});
            skLineSegment(sketch, "E154", {"start": v(-5.63, 0) * mm, "end": v(6.4, 0) * mm});
            skLineSegment(sketch, "E155", {"start": v(6.4, 0) * mm, "end": v(6.4, 2) * mm});
            skPoint(sketch, "E156", {"position": v(-5.65, 28) * mm});
            skPoint(sketch, "E157", {"position": v(5.52, 26) * mm});
            skPoint(sketch, "E158", {"position": v(-5.65, 26) * mm});
            skLineSegment(sketch, "E159", {"start": v(-5.65, 28) * mm, "end": v(-5.65, 26) * mm});
            skLineSegment(sketch, "E160", {"start": v(-5.65, 26) * mm, "end": v(6.5, 26) * mm});
            skLineSegment(sketch, "E161", {"start": v(6.5, 26) * mm, "end": v(5.52, 26) * mm});
            skSolve(sketch);
        }
        {
            var Q0;
            Q0 = qSketchRegion(id + "F26", true);
            var Q1;
            {var subQ1=sQuery(id+"F26.wireOp",EDGE,"E160");Q1=makeQuery(id+"F26.imprint","IMPRINT",FACE,{"disambiguationData":[TD([[makeQuery(id+"F26.imprint","IMPRINT",EDGE,{"derivedFrom":subQ1}),1.0]])]});}
            extrude(context, id + "F27", {"entities" : qUnion([Q0, Q1]), "operationType" : NewBodyOperationType.ADD, "depth" : 16 * mm});
        }
        {
            var Q0;
            {var subQ0=sQuery(id+"F0.wireOp",EDGE,"E0.1");Q0=makeQuery(id+"F0.imprint","IMPRINT",FACE,{"disambiguationData":[TD([[makeQuery(id+"F0.imprint","IMPRINT",EDGE,{"derivedFrom":subQ0}),1.0]])]});}
            var sketch = newSketch(context, id + "F28", { "sketchPlane" : qUnion([Q0])});
            skPoint(sketch, "E162", {"position": v(1.79, -1.92) * mm});
            skPoint(sketch, "E163", {"position": v(1.79, 2.08) * mm});
            skLineSegment(sketch, "E164", {"start": v(1.79, 2.08) * mm, "end": v(1.79, -1.92) * mm});
            skLineSegment(sketch, "E165", {"start": v(1.79, -1.92) * mm, "end": v(3.79, -1.92) * mm});
            skLineSegment(sketch, "E166", {"start": v(3.79, -1.92) * mm, "end": v(3.79, 2.08) * mm});
            skLineSegment(sketch, "E167", {"start": v(3.79, 2.08) * mm, "end": v(1.79, 2.08) * mm});
            skSolve(sketch);
        }
        {
            var Q0;
            Q0=makeQuery(id+"F28.imprint","IMPRINT",FACE,{"disambiguationData":[TD([[makeQuery(id+"F28.imprint","IMPRINT",EDGE,{"derivedFrom":sQuery(id+"F28.wireOp",EDGE,"E164")}),1.0]])]});
            extrude(context, id + "F29", {"entities" : qUnion([Q0]), "operationType" : NewBodyOperationType.REMOVE, "depth" : 2 * mm});
        }
        {
            var Q0;
            {var subQ0=sQuery(id+"F0.wireOp",EDGE,"E15");var subQ1=sQuery(id+"F0.wireOp",EDGE,"E13");var subQ2=sQuery(id+"F0.wireOp",EDGE,"E0.3");Q0=makeQuery(id+"F27.boolean.opBoolean","MERGE",FACE,{"derivedFrom":[makeQuery(id+"F1.opExtrude","SWEPT_FACE",FACE,{"disambiguationData":[OSD([subQ2]),TDD([makeQuery(id+"F0.imprint","IMPRINT",EDGE,{"disambiguationData":[TD([[makeQuery(id+"F0.imprint","INTERSECT",VERTEX,{"derivedFrom":[subQ2,subQ0]}),1.0]])],"derivedFrom":subQ2})])]}),makeQuery(id+"F8.boolean.opBoolean","MERGE",FACE,{"derivedFrom":[makeQuery(id+"F6.boolean.opBoolean","MERGE",FACE,{"derivedFrom":[makeQuery(id+"F1.opExtrude","SWEPT_FACE",FACE,{"disambiguationData":[OSD([subQ2]),TDD([makeQuery(id+"F0.imprint","IMPRINT",EDGE,{"disambiguationData":[TD([[makeQuery(id+"F0.imprint","INTERSECT",VERTEX,{"derivedFrom":[sQuery(id+"F0.wireOp",EDGE,"E0.2"),subQ2]}),1.0]])],"derivedFrom":subQ2})])]}),makeQuery(id+"F6.opExtrude","SWEPT_FACE",FACE,{"disambiguationData":[OSD([sQuery(id+"F5.wireOp",EDGE,"E39")])]})]}),makeQuery(id+"F8.opExtrude","SWEPT_FACE",FACE,{"disambiguationData":[OSD([sQuery(id+"F7.wireOp",EDGE,"E53.MirrorCS")])]})]}),makeQuery(id+"F27.opExtrude","CAP_FACE",FACE,{"disambiguationData":[OSD([sQuery(id+"F26.wireOp",EDGE,"E152"),sQuery(id+"F26.wireOp",EDGE,"E153"),sQuery(id+"F26.wireOp",EDGE,"E154"),sQuery(id+"F26.wireOp",EDGE,"E155")])],"isStart":false}),makeQuery(id+"F27.opExtrude","CAP_FACE",FACE,{"disambiguationData":[OSD([subQ1,sQuery(id+"F0.wireOp",EDGE,"E14"),subQ0,sQuery(id+"F26.wireOp",EDGE,"E160"),sQuery(id+"F26.wireOp",EDGE,"E161")])],"isStart":false})]});}
            var sketch = newSketch(context, id + "F30", { "sketchPlane" : qUnion([Q0])});
            skLineSegment(sketch, "E168", {"start": v(-19.6, 33) * mm, "end": v(-19.6, 34) * mm, "construction": true});
            skFitSpline(sketch, "E169", {"points": [v(-22.1, 33) * mm, v(-19.6, 34) * mm, v(-16.06, 31.54) * mm], "startDerivative": vector(3.05, 7.72) * mm, "endDerivative": vector(5.72, -11.1) * mm});
            skLineSegment(sketch, "E170", {"start": v(-22.1, 33) * mm, "end": v(-26.1, 33) * mm});
            skLineSegment(sketch, "E171", {"start": v(-26.1, 33) * mm, "end": v(-26.1, 34) * mm});
            skLineSegment(sketch, "E172", {"start": v(-26.1, 34) * mm, "end": v(-19.6, 34) * mm});
            skSolve(sketch);
        }
        {
            var Q0;
            {var subQ0=sQuery(id+"F30.wireOp",EDGE,"9izlcW5J-VZdE-enLE-zUEK-5Wq35H0GoYl3");var subQ1=makeQuery(id+"F30.imprint","INTERSECT",VERTEX,{"derivedFrom":[subQ0,sQuery(id+"F30.wireOp",EDGE,"E169")]});Q0=makeQuery(id+"F30.imprint","IMPRINT",FACE,{"disambiguationData":[TD([[makeQuery(id+"F30.imprint","IMPRINT",EDGE,{"disambiguationData":[TD([[subQ1,-1.0]])],"derivedFrom":subQ0}),1.0]])]});}
            var Q1;
            {var subQ5=sQuery(id+"F30.wireOp",EDGE,"E169");Q1=makeQuery(id+"F30.imprint","IMPRINT",FACE,{"disambiguationData":[TD([[makeQuery(id+"F30.imprint","IMPRINT",EDGE,{"derivedFrom":subQ5}),-1.0]])]});}
            var Q2;
            Q2=makeQuery(id+"F30.imprint","IMPRINT",FACE,{"disambiguationData":[TD([[makeQuery(id+"F30.imprint","IMPRINT",EDGE,{"derivedFrom":sQuery(id+"F30.wireOp",EDGE,"E170")}),-1.0]])]});
            extrude(context, id + "F31", {"entities" : qUnion([Q0, Q1, Q2]), "operationType" : NewBodyOperationType.ADD, "oppositeDirection" : true, "depth" : 32 * mm});
        }
        {
            var Q0;
            {var subQ1=sQuery(id+"F13.wireOp",EDGE,"E93.MirrorCS");var subQ2=makeQuery(id+"F14.opExtrude","SWEPT_EDGE",EDGE,{"disambiguationData":[OSD([sQuery(id+"F13.wireOp",EDGE,"E92.MirrorCS"),subQ1])]});Q0=makeQuery(id+"F15.imprint","IMPRINT",FACE,{"disambiguationData":[TD([[makeQuery(id+"F15.imprint","IMPRINT",EDGE,{"derivedFrom":subQ2}),1.0]])]});}
            extrude(context, id + "F32", {"entities" : qUnion([Q0]), "operationType" : NewBodyOperationType.REMOVE, "oppositeDirection" : true, "depth" : 25 * mm});
        }
        {
            var Q0;
            {var subQ4=sQuery(id+"F15.wireOp",EDGE,"E106");Q0=makeQuery(id+"F15.imprint","IMPRINT",FACE,{"disambiguationData":[TD([[makeQuery(id+"F15.imprint","IMPRINT",EDGE,{"derivedFrom":subQ4}),1.0]])]});}
            var Q1;
            {var subQ0=sQuery(id+"F15.wireOp",EDGE,"E104");var subQ3=sQuery(id+"F15.wireOp",EDGE,"E111");var subQ4=makeQuery(id+"F15.imprint","INTERSECT",VERTEX,{"derivedFrom":[subQ0,subQ3]});Q1=makeQuery(id+"F15.imprint","IMPRINT",FACE,{"disambiguationData":[TD([[makeQuery(id+"F15.imprint","IMPRINT",EDGE,{"disambiguationData":[TD([[subQ4,1.0]])],"derivedFrom":subQ3}),1.0]])]});}
            extrude(context, id + "F33", {"entities" : qUnion([Q0, Q1]), "operationType" : NewBodyOperationType.ADD, "oppositeDirection" : true, "depth" : 9.5 * mm});
        }
        {
            var Q0;
            Q0=makeQuery(id+"F31.opExtrude","SWEPT_EDGE",EDGE,{"disambiguationData":[OSD([sQuery(id+"F30.wireOp",EDGE,"E171"),sQuery(id+"F30.wireOp",EDGE,"E172")])]});
            fillet(context, id + "F34", {"entities" : qUnion([Q0]), "radius" : 2 * mm, "tangentPropagation" : true, "allowEdgeOverflow" : false});
        }
        {
            var Q0;
            Q0=makeQuery(id+"F33.opExtrude","SWEPT_EDGE",EDGE,{"disambiguationData":[OSD([sQuery(id+"F15.wireOp",EDGE,"E109"),sQuery(id+"F15.wireOp",EDGE,"E110")])]});
            fillet(context, id + "F35", {"entities" : qUnion([Q0]), "radius" : 2 * mm, "tangentPropagation" : true, "allowEdgeOverflow" : false});
        }
        {
            var Q0;
            {var subQ0=sQuery(id+"F0.wireOp",EDGE,"E14");Q0=makeQuery(id+"F27.boolean.opBoolean","MERGE",FACE,{"derivedFrom":[makeQuery(id+"F6.boolean.opBoolean","MERGE",FACE,{"derivedFrom":[makeQuery(id+"F1.opExtrude","CAP_FACE",FACE,{"disambiguationData":[OSD([sQuery(id+"F0.wireOp",EDGE,"E0.0"),sQuery(id+"F0.wireOp",EDGE,"E0.1"),sQuery(id+"F0.wireOp",EDGE,"E0.2"),sQuery(id+"F0.wireOp",EDGE,"E0.3"),sQuery(id+"F0.wireOp",EDGE,"E4"),sQuery(id+"F0.wireOp",EDGE,"E5"),sQuery(id+"F0.wireOp",EDGE,"E6.MirrorCS"),sQuery(id+"F0.wireOp",EDGE,"E7.MirrorCS"),sQuery(id+"F0.wireOp",EDGE,"E9"),sQuery(id+"F0.wireOp",EDGE,"E10"),sQuery(id+"F0.wireOp",EDGE,"E11.MirrorCS"),sQuery(id+"F0.wireOp",EDGE,"E12.MirrorCS"),sQuery(id+"F0.wireOp",EDGE,"E13"),subQ0,sQuery(id+"F0.wireOp",EDGE,"E15")])],"isStart":false}),makeQuery(id+"F6.opExtrude","SWEPT_FACE",FACE,{"disambiguationData":[OSD([sQuery(id+"F5.wireOp",EDGE,"E38")])]})]}),makeQuery(id+"F27.opExtrude","SWEPT_FACE",FACE,{"disambiguationData":[OSD([subQ0])]})]});}
            var sketch = newSketch(context, id + "F36", { "sketchPlane" : qUnion([Q0])});
            skPoint(sketch, "E173", {"position": v(16.38, 10.4) * mm});
            skPoint(sketch, "E174", {"position": v(16.38, 6.4) * mm});
            skLineSegment(sketch, "E175", {"start": v(16.38, 6.4) * mm, "end": v(0.38, 6.4) * mm});
            skLineSegment(sketch, "E176", {"start": v(0.38, 6.4) * mm, "end": v(0.38, -5.6) * mm});
            skLineSegment(sketch, "E177", {"start": v(0.38, -5.6) * mm, "end": v(16.38, -5.6) * mm});
            skLineSegment(sketch, "E178", {"start": v(16.38, -5.6) * mm, "end": v(16.38, 6.4) * mm, "construction": true});
            skSolve(sketch);
        }
        {
            var Q0;
            {var subQ0=sQuery(id+"F36.wireOp",EDGE,"E175");Q0=makeQuery(id+"F36.imprint","IMPRINT",FACE,{"disambiguationData":[TD([[makeQuery(id+"F36.imprint","IMPRINT",EDGE,{"derivedFrom":subQ0}),1.0]])]});}
            extrude(context, id + "F37", {"entities" : qUnion([Q0]), "operationType" : NewBodyOperationType.REMOVE, "endBound" : BoundingType.UP_TO_NEXT, "oppositeDirection" : true, "depth" : 25 * mm});
        }
    });
